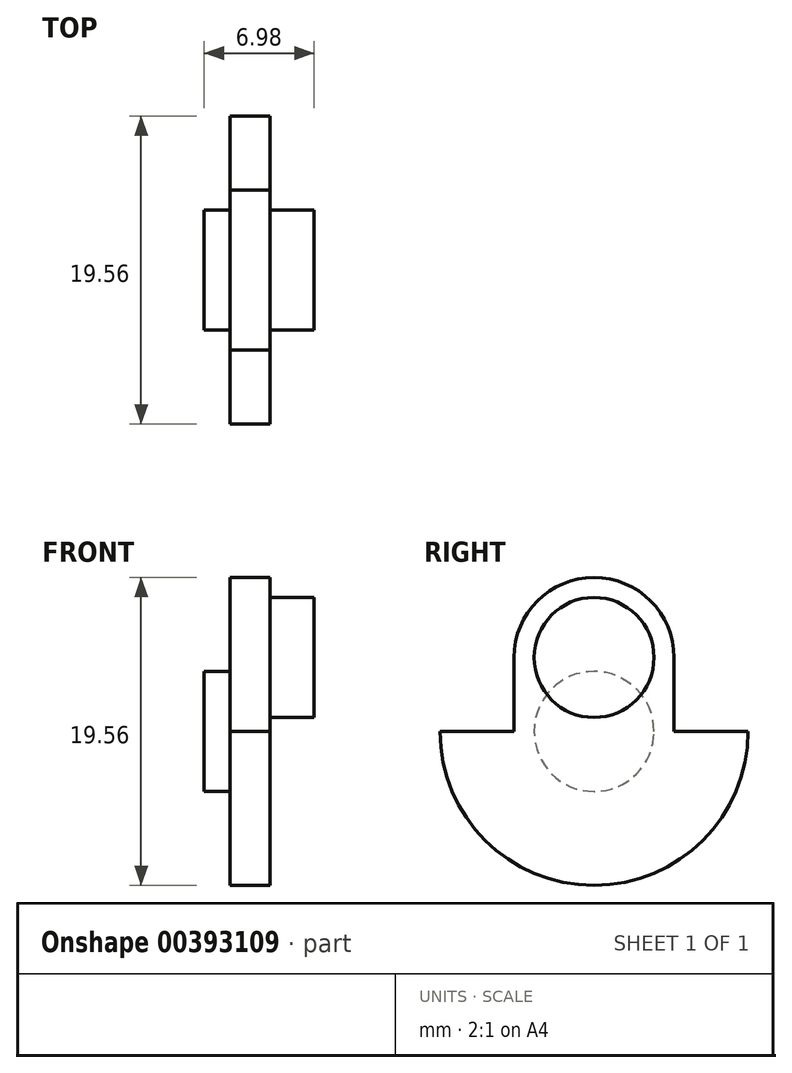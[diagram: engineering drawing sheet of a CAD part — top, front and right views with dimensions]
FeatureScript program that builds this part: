
annotation { "Feature Type Name" : "Feature", "Feature Type Description" : "" }
export const myFeature = defineFeature(function(context is Context, id is Id, definition is map)
    precondition{}
    {
        {
            var Q0;
            Q0=qCreatedBy(makeId("Right.planeOp"),FACE);
            var sketch = newSketch(context, id + "F0", { "sketchPlane" : qUnion([Q0])});
            skArc(sketch, "E0", {"start": v(5.08, 4.7) * mm, "mid": v(0, 9.78) * mm, "end": v(-5.08, 4.7) * mm});
            skArc(sketch, "E1", {"start": v(-9.78, 0) * mm, "mid": v(0, -9.78) * mm, "end": v(9.78, 0) * mm});
            skLineSegment(sketch, "E2", {"start": v(0, 0) * mm, "end": v(-9.78, 0) * mm});
            skLineSegment(sketch, "E3", {"start": v(-9.78, 0) * mm, "end": v(0, 0) * mm});
            skLineSegment(sketch, "E4", {"start": v(-5.08, 4.7) * mm, "end": v(-5.08, -6.73) * mm});
            skLineSegment(sketch, "E5", {"start": v(5.08, 4.7) * mm, "end": v(5.08, 0) * mm});
            skLineSegment(sketch, "E6.trimOffspring", {"start": v(5.08, 0) * mm, "end": v(9.78, 0) * mm});
            skSolve(sketch);
        }
        {
            var Q0;
            Q0=makeQuery(id+"F0.imprint","IMPRINT",FACE,{"disambiguationData":[TD([[makeQuery(id+"F0.imprint","IMPRINT",EDGE,{"derivedFrom":sQuery(id+"F0.wireOp",EDGE,"E0")}),1.0]])]});
            extrude(context, id + "F1", {"entities" : qUnion([Q0]), "depth" : 2.54 * mm});
        }
        {
            var Q0;
            Q0=makeQuery(id+"F1.opExtrude","CAP_FACE",FACE,{"disambiguationData":[OSD([sQuery(id+"F0.wireOp",EDGE,"E0"),sQuery(id+"F0.wireOp",EDGE,"E1"),sQuery(id+"F0.wireOp",EDGE,"E3"),sQuery(id+"F0.wireOp",EDGE,"E4"),sQuery(id+"F0.wireOp",EDGE,"E5"),sQuery(id+"F0.wireOp",EDGE,"E6.trimOffspring")])],"isStart":false});
            var sketch = newSketch(context, id + "F2", { "sketchPlane" : qUnion([Q0])});
            skCircle(sketch, "E7", {"center": v(0, 4.7) * mm, "radius": 3.81 * mm});
            skSolve(sketch);
        }
        {
            var Q0;
            Q0=makeQuery(id+"F2.imprint","IMPRINT",FACE,{"disambiguationData":[TD([[makeQuery(id+"F2.imprint","IMPRINT",EDGE,{"derivedFrom":sQuery(id+"F2.wireOp",EDGE,"E7")}),1.0]])]});
            extrude(context, id + "F3", {"entities" : qUnion([Q0]), "operationType" : NewBodyOperationType.ADD, "depth" : 2.8 * mm});
        }
        {
            var Q0;
            Q0=makeQuery(id+"F1.opExtrude","CAP_FACE",FACE,{"disambiguationData":[OSD([sQuery(id+"F0.wireOp",EDGE,"E0"),sQuery(id+"F0.wireOp",EDGE,"E1"),sQuery(id+"F0.wireOp",EDGE,"E3"),sQuery(id+"F0.wireOp",EDGE,"E4"),sQuery(id+"F0.wireOp",EDGE,"E5"),sQuery(id+"F0.wireOp",EDGE,"E6.trimOffspring")])],"isStart":true});
            var sketch = newSketch(context, id + "F4", { "sketchPlane" : qUnion([Q0])});
            skCircle(sketch, "E8", {"center": v(0, 0) * mm, "radius": 3.8 * mm});
            skSolve(sketch);
        }
        {
            var Q0;
            Q0 = qSketchRegion(id + "F4", true);
            extrude(context, id + "F5", {"entities" : qUnion([Q0]), "operationType" : NewBodyOperationType.ADD, "depth" : 1.56 * mm});
        }
        {
            var Q0;
            Q0=makeQuery(id+"F5.opExtrude","CAP_FACE",FACE,{"disambiguationData":[OSD([sQuery(id+"F4.wireOp",EDGE,"E8")])],"isStart":false});
            extrude(context, id + "F6", {"entities" : qUnion([Q0]), "operationType" : NewBodyOperationType.ADD, "depth" : 0.09 * mm});
        }
    });
